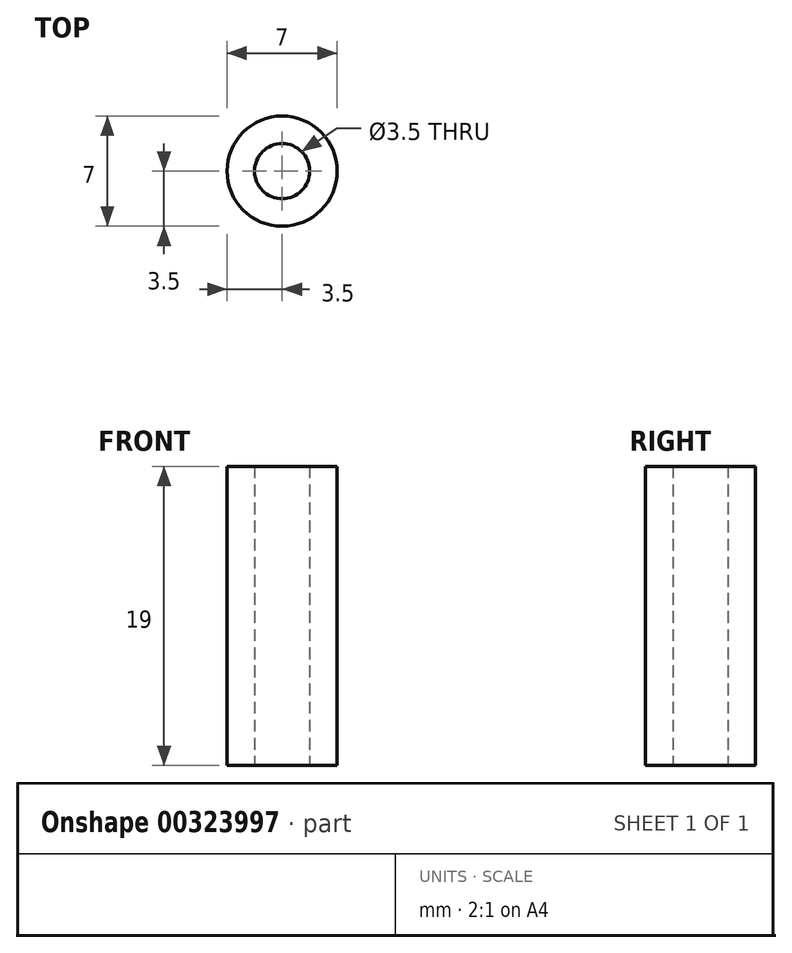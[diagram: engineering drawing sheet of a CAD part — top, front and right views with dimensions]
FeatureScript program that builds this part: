
annotation { "Feature Type Name" : "Feature", "Feature Type Description" : "" }
export const myFeature = defineFeature(function(context is Context, id is Id, definition is map)
    precondition{}
    {
        {
            var Q0;
            Q0=qCreatedBy(makeId("Top.planeOp"),FACE);
            var sketch = newSketch(context, id + "F0", { "sketchPlane" : qUnion([Q0])});
            skCircle(sketch, "E0", {"center": v(0, 0) * mm, "radius": 3.5 * mm});
            skCircle(sketch, "E1", {"center": v(0, 0) * mm, "radius": 1.75 * mm});
            skSolve(sketch);
        }
        {
            var Q0;
            Q0=makeQuery(id+"F0.imprint","IMPRINT",FACE,{"disambiguationData":[TD([[makeQuery(id+"F0.imprint","IMPRINT",EDGE,{"derivedFrom":sQuery(id+"F0.wireOp",EDGE,"E0")}),1.0]])]});
            extrude(context, id + "F1", {"entities" : qUnion([Q0]), "depth" : 19 * mm});
        }
    });
